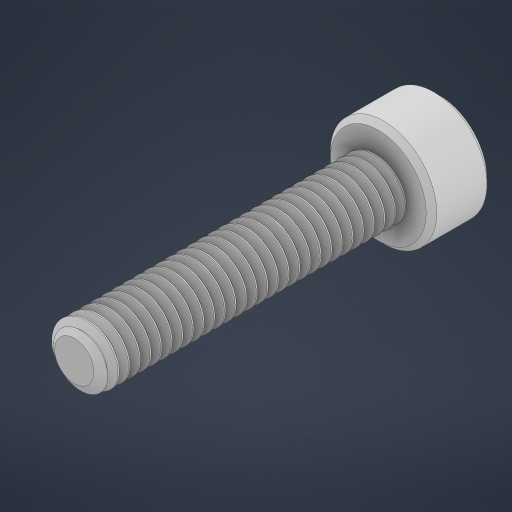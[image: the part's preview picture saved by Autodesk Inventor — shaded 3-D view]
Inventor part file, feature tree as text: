
AUTODESK INVENTOR PART (.ipt)
format: ipt  version: 2023 (Build 270158000, 158)  size: 962,048 bytes
history: native  units: in
note: dims shown in document units (in); Inventor stores cm internally (conversion verified against a paired STEP export)
features: chamfer x1
ambient origin geometry x8: Origin, YZ Plane, XZ Plane, XY Plane, X Axis, Y Axis, Z Axis, Center Point
bodies: Solid1 (feature_tree)
feature tree (1):
  chamfer  "Chamfer1"  [1 undecoded]
note: 1 required parameter value undecoded (feature->parameter linkage not recoverable at this tier; creation-order binding heuristic only, values carry confidence <= 0.55)
